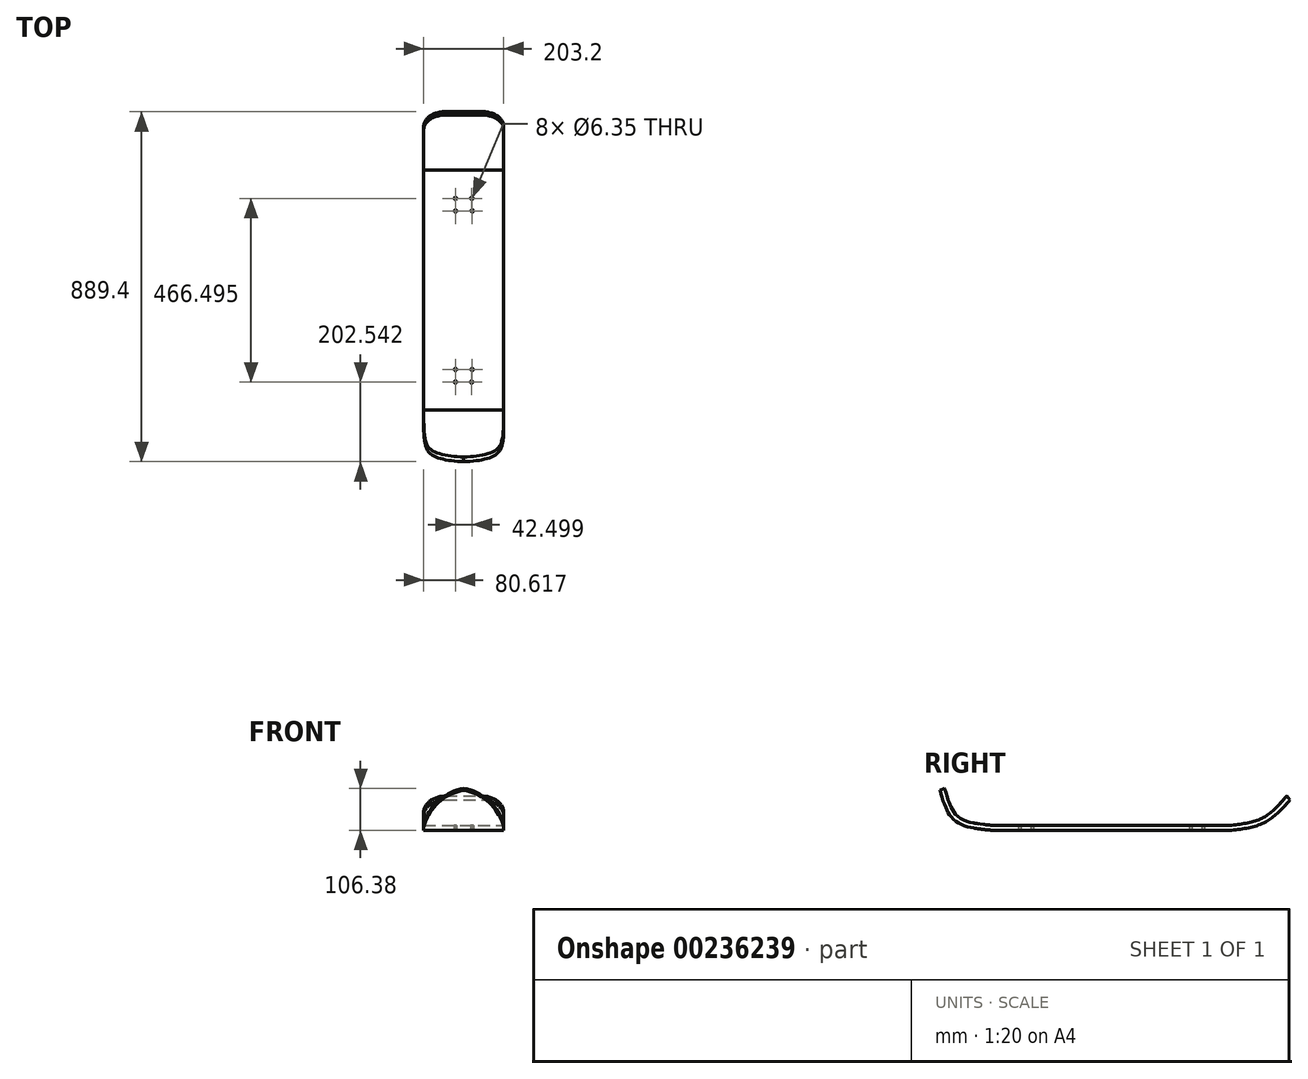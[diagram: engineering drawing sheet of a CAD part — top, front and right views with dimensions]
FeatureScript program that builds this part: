
annotation { "Feature Type Name" : "Feature", "Feature Type Description" : "" }
export const myFeature = defineFeature(function(context is Context, id is Id, definition is map)
    precondition{}
    {
        {
            var Q0;
            Q0=qCreatedBy(makeId("Top.planeOp"),FACE);
            var sketch = newSketch(context, id + "F0", { "sketchPlane" : qUnion([Q0])});
            skLineSegment(sketch, "E0.bottom", {"start": v(-101.6, -304.8) * mm, "end": v(101.6, -304.8) * mm});
            skLineSegment(sketch, "E0.top", {"start": v(-101.6, 304.8) * mm, "end": v(101.6, 304.8) * mm});
            skLineSegment(sketch, "E0.left", {"start": v(-101.6, -304.8) * mm, "end": v(-101.6, 304.8) * mm});
            skLineSegment(sketch, "E0.right", {"start": v(101.6, -304.8) * mm, "end": v(101.6, 304.8) * mm});
            skPoint(sketch, "E0.middle", {"position": v(0, 0) * mm});
            skPoint(sketch, "E1.middle", {"position": v(0, 217.37) * mm});
            skCircle(sketch, "E2", {"center": v(-20.98, 233.25) * mm, "radius": 3.18 * mm});
            skCircle(sketch, "E3", {"center": v(20.36, 233.25) * mm, "radius": 3.18 * mm});
            skCircle(sketch, "E4", {"center": v(-20.8, 201.5) * mm, "radius": 3.18 * mm});
            skCircle(sketch, "E5", {"center": v(21.52, 201.5) * mm, "radius": 3.18 * mm});
            skPoint(sketch, "E1.right.end.orphan", {"position": v(25.4, 242.77) * mm});
            skPoint(sketch, "E1.bottom.end.orphan", {"position": v(25.4, 191.97) * mm});
            skPoint(sketch, "E1.left.end.orphan", {"position": v(-25.4, 242.77) * mm});
            skPoint(sketch, "E1.left.start.orphan", {"position": v(-25.4, 191.97) * mm});
            skCircle(sketch, "E6.MirrorC", {"center": v(-20.8, -201.5) * mm, "radius": 3.18 * mm});
            skCircle(sketch, "E7.MirrorC", {"center": v(-20.98, -233.25) * mm, "radius": 3.18 * mm});
            skCircle(sketch, "E8.MirrorC", {"center": v(20.36, -233.25) * mm, "radius": 3.18 * mm});
            skCircle(sketch, "E9.MirrorC", {"center": v(21.52, -201.5) * mm, "radius": 3.18 * mm});
            skSolve(sketch);
        }
        {
            var Q0;
            Q0=makeQuery(id+"F0.imprint","IMPRINT",FACE,{"disambiguationData":[TD([[makeQuery(id+"F0.imprint","IMPRINT",EDGE,{"derivedFrom":sQuery(id+"F0.wireOp",EDGE,"E0.bottom")}),1.0]])]});
            extrude(context, id + "F1", {"entities" : qUnion([Q0]), "endBound" : BoundingType.SYMMETRIC, "depth" : 12.7 * mm});
        }
        {
            var Q0;
            Q0=qCreatedBy(makeId("Right.planeOp"),FACE);
            var sketch = newSketch(context, id + "F2", { "sketchPlane" : qUnion([Q0])});
            skFitSpline(sketch, "E10", {"points": [v(304.76, 0) * mm, v(370, 12.34) * mm, v(413.5, 38.2) * mm, v(449.35, 75.82) * mm], "startDerivative": vector(190.16, 23.04) * mm, "endDerivative": vector(107.56, 123.8) * mm});
            skSolve(sketch);
        }
        {
            var Q0;
            Q0=makeQuery(id+"F1.opExtrude","SWEPT_FACE",FACE,{"disambiguationData":[OSD([sQuery(id+"F0.wireOp",EDGE,"E0.top")])]});
            var Q1;
            Q1=sQuery(id+"F2.wireOp",EDGE,"E10");
            sweep(context, id + "F3", {"operationType" : NewBodyOperationType.ADD, "profiles" : qUnion([Q0]), "path" : qUnion([Q1])});
        }
        {
            var Q0;
            Q0=qCreatedBy(makeId("Right.planeOp"),FACE);
            var sketch = newSketch(context, id + "F4", { "sketchPlane" : qUnion([Q0])});
            skFitSpline(sketch, "E11", {"points": [v(-306.94, 0) * mm, v(-389.58, 19.73) * mm, v(-418.83, 62.15) * mm, v(-431.13, 101.5) * mm], "startDerivative": vector(-233.96, 23.59) * mm, "endDerivative": vector(-37.47, 136.38) * mm});
            skSolve(sketch);
        }
        {
            var Q0;
            Q0=makeQuery(id+"F1.opExtrude","SWEPT_FACE",FACE,{"disambiguationData":[OSD([sQuery(id+"F0.wireOp",EDGE,"E0.bottom")])]});
            var Q1;
            Q1=sQuery(id+"F4.wireOp",EDGE,"E11");
            sweep(context, id + "F5", {"operationType" : NewBodyOperationType.ADD, "profiles" : qUnion([Q0]), "path" : qUnion([Q1])});
        }
        {
            var Q0;
            Q0=makeQuery(id+"F5.opSweep","CAP_EDGE",EDGE,{"disambiguationData":[OSD([sQuery(id+"F0.wireOp",EDGE,"E0.bottom"),sQuery(id+"F0.wireOp",EDGE,"E0.left"),sQuery(id+"F4.wireOp",VERTEX,"E11.end")])],"isStart":false});
            var Q1;
            Q1=makeQuery(id+"F5.opSweep","CAP_EDGE",EDGE,{"disambiguationData":[OSD([sQuery(id+"F0.wireOp",EDGE,"E0.bottom"),sQuery(id+"F0.wireOp",EDGE,"E0.right"),sQuery(id+"F4.wireOp",VERTEX,"E11.end")])],"isStart":false});
            fillet(context, id + "F6", {"entities" : qUnion([Q0, Q1]), "radius" : 122.64 * mm, "tangentPropagation" : true, "allowEdgeOverflow" : false});
        }
        {
            var Q0;
            Q0=makeQuery(id+"F3.opSweep","CAP_EDGE",EDGE,{"disambiguationData":[OSD([sQuery(id+"F0.wireOp",EDGE,"E0.top"),sQuery(id+"F0.wireOp",EDGE,"E0.right"),sQuery(id+"F2.wireOp",VERTEX,"E10.end")])],"isStart":false});
            var Q1;
            Q1=makeQuery(id+"F3.opSweep","CAP_EDGE",EDGE,{"disambiguationData":[OSD([sQuery(id+"F0.wireOp",EDGE,"E0.top"),sQuery(id+"F0.wireOp",EDGE,"E0.left"),sQuery(id+"F2.wireOp",VERTEX,"E10.end")])],"isStart":false});
            fillet(context, id + "F7", {"entities" : qUnion([Q0, Q1]), "radius" : 55.19 * mm, "tangentPropagation" : true, "allowEdgeOverflow" : false});
        }
    });
